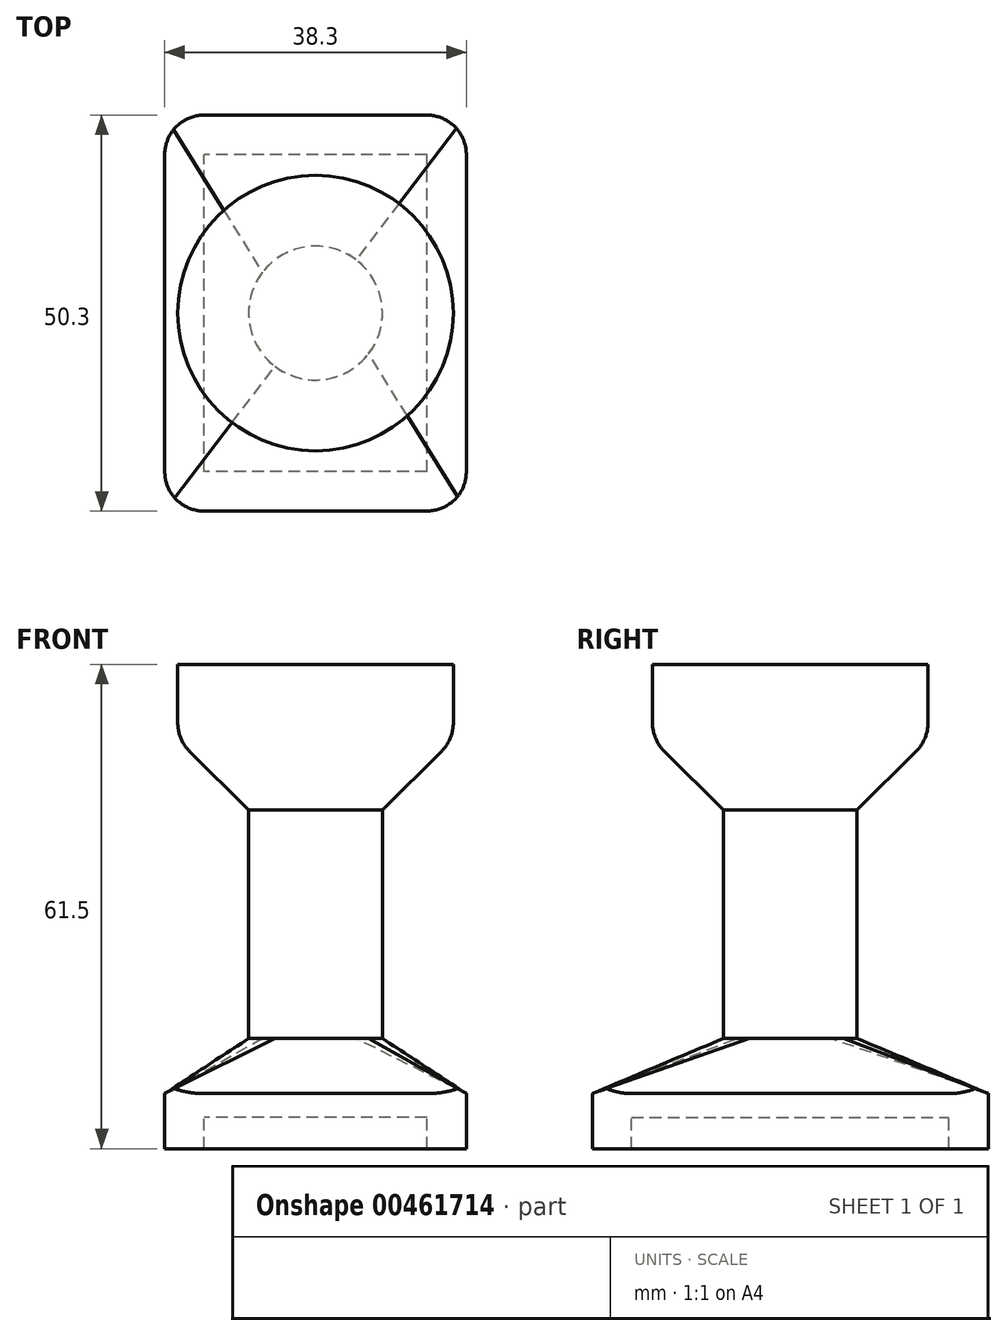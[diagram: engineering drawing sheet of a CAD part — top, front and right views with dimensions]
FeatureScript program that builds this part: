
annotation { "Feature Type Name" : "Feature", "Feature Type Description" : "" }
export const myFeature = defineFeature(function(context is Context, id is Id, definition is map)
    precondition{}
    {
        {
            var Q0;
            Q0=qCreatedBy(makeId("Top.planeOp"),FACE);
            var sketch = newSketch(context, id + "F0", { "sketchPlane" : qUnion([Q0])});
            skLineSegment(sketch, "E0.bottom", {"start": v(14.15, -20.15) * mm, "end": v(-14.15, -20.15) * mm});
            skLineSegment(sketch, "E0.top", {"start": v(14.15, 20.15) * mm, "end": v(-14.15, 20.15) * mm});
            skLineSegment(sketch, "E0.left", {"start": v(14.15, -20.15) * mm, "end": v(14.15, 20.15) * mm});
            skLineSegment(sketch, "E0.right", {"start": v(-14.15, -20.15) * mm, "end": v(-14.15, 20.15) * mm});
            skPoint(sketch, "E0.middle", {"position": v(0, 0) * mm});
            skLineSegment(sketch, "E1.0", {"start": v(19.15, 25.15) * mm, "end": v(-19.15, 25.15) * mm});
            skLineSegment(sketch, "E1.1", {"start": v(19.15, -25.15) * mm, "end": v(19.15, 25.15) * mm});
            skLineSegment(sketch, "E1.2", {"start": v(19.15, -25.15) * mm, "end": v(-19.15, -25.15) * mm});
            skLineSegment(sketch, "E1.3", {"start": v(-19.15, -25.15) * mm, "end": v(-19.15, 25.15) * mm});
            skSolve(sketch);
        }
        {
            var Q0;
            Q0=qCreatedBy(makeId("Top.planeOp"),FACE);
            cPlane(context, id + "F1", {"entities" : qUnion([Q0]), "cplaneType" : CPlaneType.OFFSET, "offset" : 10 * mm, "width" : 150 * mm, "height" : 150 * mm});
        }
        {
            var Q0;
            Q0=qCreatedBy(id+"F1.planeOp",FACE);
            var sketch = newSketch(context, id + "F2", { "sketchPlane" : qUnion([Q0])});
            skCircle(sketch, "E2", {"center": v(0, 0) * mm, "radius": 8.5 * mm});
            skSolve(sketch);
        }
        {
            var Q0;
            Q0=qCreatedBy(makeId("Front.planeOp"),FACE);
            var sketch = newSketch(context, id + "F3", { "sketchPlane" : qUnion([Q0])});
            skCircle(sketch, "E3", {"center": v(0, 48) * mm, "radius": 17.5 * mm});
            skLineSegment(sketch, "E4", {"start": v(0, 65.5) * mm, "end": v(0, 30.5) * mm});
            skLineSegment(sketch, "E5", {"start": v(0, 30.5) * mm, "end": v(-17.5, 48) * mm});
            skLineSegment(sketch, "E6", {"start": v(-17.5, 48) * mm, "end": v(-17.5, 65.5) * mm});
            skLineSegment(sketch, "E7", {"start": v(-17.5, 65.5) * mm, "end": v(0, 65.5) * mm});
            skSolve(sketch);
        }
        {
            var Q0;
            Q0=makeQuery(id+"F0.imprint","IMPRINT",FACE,{"disambiguationData":[TD([[makeQuery(id+"F0.imprint","IMPRINT",EDGE,{"derivedFrom":sQuery(id+"F0.wireOp",EDGE,"E0.bottom")}),1.0]])]});
            extrude(context, id + "F4", {"entities" : qUnion([Q0]), "oppositeDirection" : true, "depth" : 4 * mm});
        }
        {
            var Q0;
            Q0 = qSketchRegion(id + "F0", true);
            var Q1;
            Q1=makeQuery(id+"F0.imprint","IMPRINT",FACE,{"disambiguationData":[TD([[makeQuery(id+"F0.imprint","IMPRINT",EDGE,{"derivedFrom":sQuery(id+"F0.wireOp",EDGE,"E0.bottom")}),-1.0]])]});
            extrude(context, id + "F5", {"entities" : qUnion([Q0, Q1]), "operationType" : NewBodyOperationType.ADD, "depth" : 3 * mm});
        }
        {
            var Q1;
            Q1=makeQuery(id+"F5.opExtrude","CAP_FACE",FACE,{"disambiguationData":[OSD([sQuery(id+"F0.wireOp",EDGE,"E1.0"),sQuery(id+"F0.wireOp",EDGE,"E1.1"),sQuery(id+"F0.wireOp",EDGE,"E1.2"),sQuery(id+"F0.wireOp",EDGE,"E1.3")])],"isStart":false});
            var Q2;
            Q2=makeQuery(id+"F2.imprint","IMPRINT",FACE,{"disambiguationData":[TD([[makeQuery(id+"F2.imprint","IMPRINT",EDGE,{"derivedFrom":sQuery(id+"F2.wireOp",EDGE,"E2")}),1.0]])]});
            loft(context, id + "F6", {"operationType" : NewBodyOperationType.ADD, "sheetProfilesArray" : [{ "sheetProfileEntities" : qUnion([Q1]) }, { "sheetProfileEntities" : qUnion([Q2]) }]});
        }
        {
            var Q0;
            Q0=makeQuery(id+"F6.opLoft","CAP_FACE",FACE,{"disambiguationData":[OSD([makeQuery(id+"F2.imprint","IMPRINT",FACE,{"disambiguationData":[TD([[makeQuery(id+"F2.imprint","IMPRINT",EDGE,{"derivedFrom":sQuery(id+"F2.wireOp",EDGE,"E2")}),1.0]])]})])],"isStart":true});
            extrude(context, id + "F7", {"entities" : qUnion([Q0]), "operationType" : NewBodyOperationType.ADD, "depth" : 35 * mm});
        }
        {
            var Q0;
            {var subQ0=sQuery(id+"F3.wireOp",EDGE,"E4");Q0=makeQuery(id+"F3.imprint","IMPRINT",FACE,{"disambiguationData":[TD([[makeQuery(id+"F3.imprint","IMPRINT",EDGE,{"derivedFrom":subQ0}),-1.0]])]});}
            var Q1;
            {var subQ2=sQuery(id+"F3.wireOp",EDGE,"E6");Q1=makeQuery(id+"F3.imprint","IMPRINT",FACE,{"disambiguationData":[TD([[makeQuery(id+"F3.imprint","IMPRINT",EDGE,{"derivedFrom":subQ2}),-1.0]])]});}
            var Q2;
            Q2=sQuery(id+"F3.wireOp",EDGE,"E4");
            revolve(context, id + "F8", {"operationType" : NewBodyOperationType.ADD, "entities" : qUnion([Q0, Q1]), "axis" : qUnion([Q2]), "revolveType" : RevolveType.FULL});
        }
        {
            var Q0;
            Q0=makeQuery(id+"F8.opRevolve","SWEPT_FACE",FACE,{"disambiguationData":[OSD([sQuery(id+"F3.wireOp",EDGE,"E7")])]});
            extrude(context, id + "F9", {"entities" : qUnion([Q0]), "operationType" : NewBodyOperationType.REMOVE, "oppositeDirection" : true, "depth" : 8 * mm});
        }
        {
            var Q0;
            Q0=makeQuery(id+"F9.boolean.opBoolean","COPY",EDGE,{"derivedFrom":makeQuery(id+"F9.opExtrude","CAP_EDGE",EDGE,{"disambiguationData":[OSD([sQuery(id+"F3.wireOp",EDGE,"E6"),sQuery(id+"F3.wireOp",EDGE,"E7")])],"isStart":false})});
            var Q1;
            Q1=makeQuery(id+"F8.opRevolve","SWEPT_EDGE",EDGE,{"disambiguationData":[OSD([sQuery(id+"F3.wireOp",EDGE,"E3"),sQuery(id+"F3.wireOp",EDGE,"E5"),sQuery(id+"F3.wireOp",EDGE,"E6")])]});
            fillet(context, id + "F10", {"entities" : qUnion([Q0, Q1]), "radius" : 5 * mm, "tangentPropagation" : true, "allowEdgeOverflow" : false});
        }
        {
            var Q0;
            {var subQ0=sQuery(id+"F0.wireOp",EDGE,"E1.3");var subQ1=sQuery(id+"F0.wireOp",EDGE,"E1.2");Q0=makeQuery(id+"F5.boolean.opBoolean","MERGE",EDGE,{"derivedFrom":[makeQuery(id+"F4.opExtrude","SWEPT_EDGE",EDGE,{"disambiguationData":[OSD([subQ1,subQ0])]}),makeQuery(id+"F5.opExtrude","SWEPT_EDGE",EDGE,{"disambiguationData":[OSD([subQ1,subQ0])]})]});}
            var Q1;
            {var subQ0=sQuery(id+"F0.wireOp",EDGE,"E1.3");var subQ1=sQuery(id+"F0.wireOp",EDGE,"E1.0");Q1=makeQuery(id+"F5.boolean.opBoolean","MERGE",EDGE,{"derivedFrom":[makeQuery(id+"F4.opExtrude","SWEPT_EDGE",EDGE,{"disambiguationData":[OSD([subQ1,subQ0])]}),makeQuery(id+"F5.opExtrude","SWEPT_EDGE",EDGE,{"disambiguationData":[OSD([subQ1,subQ0])]})]});}
            var Q2;
            {var subQ0=sQuery(id+"F0.wireOp",EDGE,"E1.1");var subQ1=sQuery(id+"F0.wireOp",EDGE,"E1.0");Q2=makeQuery(id+"F5.boolean.opBoolean","MERGE",EDGE,{"derivedFrom":[makeQuery(id+"F4.opExtrude","SWEPT_EDGE",EDGE,{"disambiguationData":[OSD([subQ1,subQ0])]}),makeQuery(id+"F5.opExtrude","SWEPT_EDGE",EDGE,{"disambiguationData":[OSD([subQ1,subQ0])]})]});}
            var Q3;
            {var subQ0=sQuery(id+"F0.wireOp",EDGE,"E1.2");var subQ1=sQuery(id+"F0.wireOp",EDGE,"E1.1");Q3=makeQuery(id+"F5.boolean.opBoolean","MERGE",EDGE,{"derivedFrom":[makeQuery(id+"F4.opExtrude","SWEPT_EDGE",EDGE,{"disambiguationData":[OSD([subQ1,subQ0])]}),makeQuery(id+"F5.opExtrude","SWEPT_EDGE",EDGE,{"disambiguationData":[OSD([subQ1,subQ0])]})]});}
            fillet(context, id + "F11", {"entities" : qUnion([Q0, Q1, Q2, Q3]), "radius" : 5 * mm, "tangentPropagation" : true, "allowEdgeOverflow" : false});
        }
    });
